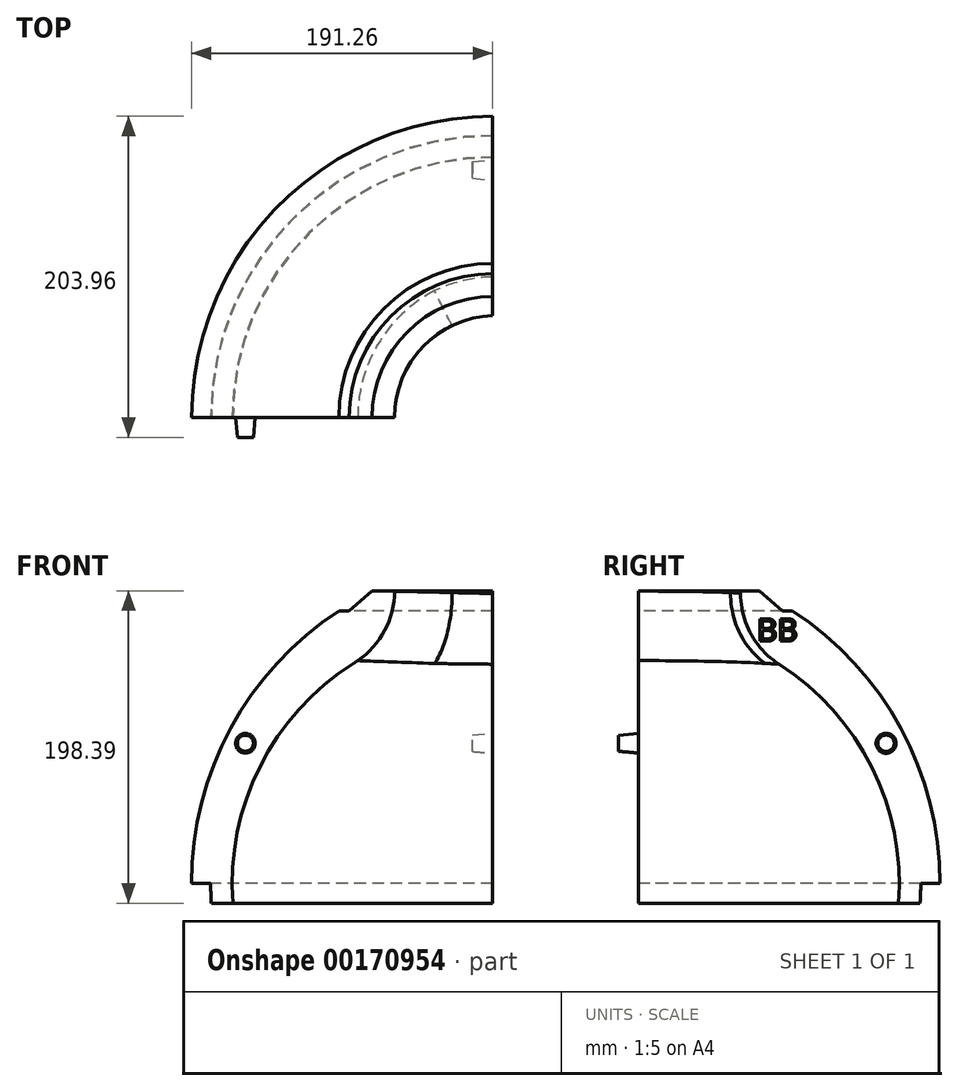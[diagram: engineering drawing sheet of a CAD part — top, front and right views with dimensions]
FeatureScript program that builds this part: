
annotation { "Feature Type Name" : "Feature", "Feature Type Description" : "" }
export const myFeature = defineFeature(function(context is Context, id is Id, definition is map)
    precondition{}
    {
        {
            var Q0;
            Q0=qCreatedBy(makeId("Front.planeOp"),FACE);
            var sketch = newSketch(context, id + "F0", { "sketchPlane" : qUnion([Q0])});
            skLineSegment(sketch, "E0", {"start": v(30.93, 103.48) * mm, "end": v(-45.8, 103.48) * mm});
            skLineSegment(sketch, "E1", {"start": v(30.93, 103.48) * mm, "end": v(30.93, 83.03) * mm});
            skLineSegment(sketch, "E2", {"start": v(-45.8, 103.48) * mm, "end": v(-60.28, 90.79) * mm});
            skLineSegment(sketch, "E3", {"start": v(30.93, -61.93) * mm, "end": v(-133.25, -61.93) * mm});
            skLineSegment(sketch, "E4", {"start": v(-147.77, -94.91) * mm, "end": v(-134.06, -94.91) * mm});
            skLineSegment(sketch, "E5", {"start": v(-160.33, -82.21) * mm, "end": v(-148.2, -82.22) * mm});
            skArc(sketch, "E6", {"start": v(-57.6, 57.35) * mm, "mid": v(-108.8, 6.19) * mm, "end": v(-133.25, -61.93) * mm});
            skArc(sketch, "E7.trimOffspring", {"start": v(-148.2, -82.22) * mm, "mid": v(-148.1, -88.57) * mm, "end": v(-147.77, -94.91) * mm});
            skLineSegment(sketch, "E8", {"start": v(30.93, 83.03) * mm, "end": v(30.93, -61.93) * mm});
            skLineSegment(sketch, "E9", {"start": v(-18.26, 103.48) * mm, "end": v(-18.26, 103.48) * mm});
            skArc(sketch, "E10", {"start": v(-66.85, 90.79) * mm, "mid": v(-135.53, 16.14) * mm, "end": v(-160.33, -82.21) * mm});
            skArc(sketch, "E11.filletArc", {"start": v(-57.6, 57.35) * mm, "mid": v(-34.45, 77.44) * mm, "end": v(-18.26, 103.48) * mm});
            skArc(sketch, "E12", {"start": v(-133.25, -61.93) * mm, "mid": v(-134.48, -78.4) * mm, "end": v(-134.06, -94.91) * mm});
            skLineSegment(sketch, "E13", {"start": v(-60.28, 90.79) * mm, "end": v(-66.85, 90.79) * mm});
            skSolve(sketch);
        }
        {
            var Q0;
            {var subQ0=sQuery(id+"F0.wireOp",EDGE,"E2");Q0=makeQuery(id+"F0.imprint","IMPRINT",FACE,{"disambiguationData":[TD([[makeQuery(id+"F0.imprint","IMPRINT",EDGE,{"derivedFrom":subQ0}),1.0]])]});}
            var Q1;
            Q1=sQuery(id+"F0.wireOp",EDGE,"E8");
            revolve(context, id + "F1", {"entities" : qUnion([Q0]), "axis" : qUnion([Q1]), "revolveType" : RevolveType.ONE_DIRECTION, "angle" : 90 * degree});
        }
        {
            var Q0;
            Q0=makeQuery(id+"F1.opRevolve","CAP_FACE",FACE,{"disambiguationData":[OSD([sQuery(id+"F0.wireOp",EDGE,"E0"),sQuery(id+"F0.wireOp",EDGE,"8f814b49-d637-47c4-8b9a-070ca617951d"),sQuery(id+"F0.wireOp",EDGE,"E2"),sQuery(id+"F0.wireOp",EDGE,"bb9fcc6d-65a5-43b8-a665-45e836ea0d68"),sQuery(id+"F0.wireOp",EDGE,"E4"),sQuery(id+"F0.wireOp",EDGE,"E5"),sQuery(id+"F0.wireOp",EDGE,"E6"),sQuery(id+"F0.wireOp",EDGE,"3126052c-2f44-435f-8919-2bff36e23e4e.trimOffspring"),sQuery(id+"F0.wireOp",EDGE,"E7.trimOffspring"),sQuery(id+"F0.wireOp",EDGE,"E9"),sQuery(id+"F0.wireOp",EDGE,"E10")])],"isStart":true});
            var sketch = newSketch(context, id + "F2", { "sketchPlane" : qUnion([Q0])});
            skCircle(sketch, "E14", {"center": v(-126.16, 6.69) * mm, "radius": 6.22 * mm});
            skSolve(sketch);
        }
        {
            var Q0;
            Q0 = qSketchRegion(id + "F2", true);
            extrude(context, id + "F3", {"entities" : qUnion([Q0]), "operationType" : NewBodyOperationType.ADD, "depth" : 12.7 * mm, "hasDraft" : true, "draftAngle" : 5 * degree, "draftPullDirection" : true});
        }
        {
            var Q0;
            Q0=makeQuery(id+"F1.opRevolve","CAP_FACE",FACE,{"disambiguationData":[OSD([sQuery(id+"F0.wireOp",EDGE,"E0"),sQuery(id+"F0.wireOp",EDGE,"8f814b49-d637-47c4-8b9a-070ca617951d"),sQuery(id+"F0.wireOp",EDGE,"E2"),sQuery(id+"F0.wireOp",EDGE,"bb9fcc6d-65a5-43b8-a665-45e836ea0d68"),sQuery(id+"F0.wireOp",EDGE,"E4"),sQuery(id+"F0.wireOp",EDGE,"E5"),sQuery(id+"F0.wireOp",EDGE,"E6"),sQuery(id+"F0.wireOp",EDGE,"3126052c-2f44-435f-8919-2bff36e23e4e.trimOffspring"),sQuery(id+"F0.wireOp",EDGE,"E7.trimOffspring"),sQuery(id+"F0.wireOp",EDGE,"E9"),sQuery(id+"F0.wireOp",EDGE,"E10")])],"isStart":false});
            var sketch = newSketch(context, id + "F4", { "sketchPlane" : qUnion([Q0])});
            skCircle(sketch, "E15", {"center": v(157.1, 6.69) * mm, "radius": 6.35 * mm});
            skSolve(sketch);
        }
        {
            var Q0;
            Q0 = qSketchRegion(id + "F4", true);
            extrude(context, id + "F5", {"entities" : qUnion([Q0]), "operationType" : NewBodyOperationType.REMOVE, "oppositeDirection" : true, "depth" : 12.7 * mm, "hasDraft" : true, "draftAngle" : 5 * degree, "draftPullDirection" : true});
        }
        {
            var Q0;
            Q0=qCreatedBy(makeId("Top.planeOp"),FACE);
            var sketch = newSketch(context, id + "F6", { "sketchPlane" : qUnion([Q0])});
            skCircle(sketch, "E16", {"center": v(33.28, 0) * mm, "radius": 64.74 * mm});
            skSolve(sketch);
        }
        {
            var Q0;
            Q0 = qSketchRegion(id + "F6", true);
            extrude(context, id + "F7", {"entities" : qUnion([Q0]), "operationType" : NewBodyOperationType.REMOVE, "endBound" : BoundingType.THROUGH_ALL, "depth" : 25.4 * mm});
        }
        {
            var Q0;
            Q0=makeQuery(id+"F7.boolean.opBoolean","INTERSECT",EDGE,{"derivedFrom":[makeQuery(id+"F1.opRevolve","SWEPT_FACE",FACE,{"disambiguationData":[OSD([sQuery(id+"F0.wireOp",EDGE,"E11.filletArc")])]}),makeQuery(id+"F7.opExtrude","SWEPT_FACE",FACE,{"disambiguationData":[OSD([sQuery(id+"F6.wireOp",EDGE,"E16")])]})]});
            fillet(context, id + "F8", {"entities" : qUnion([Q0]), "radius" : 53.34 * mm, "tangentPropagation" : true, "allowEdgeOverflow" : false});
        }
        {
            var Q0;
            Q0=makeQuery(id+"F1.opRevolve","CAP_FACE",FACE,{"disambiguationData":[OSD([sQuery(id+"F0.wireOp",EDGE,"E0"),sQuery(id+"F0.wireOp",EDGE,"E2"),sQuery(id+"F0.wireOp",EDGE,"E4"),sQuery(id+"F0.wireOp",EDGE,"E5"),sQuery(id+"F0.wireOp",EDGE,"E6"),sQuery(id+"F0.wireOp",EDGE,"E7.trimOffspring"),sQuery(id+"F0.wireOp",EDGE,"E10"),sQuery(id+"F0.wireOp",EDGE,"E11.filletArc"),sQuery(id+"F0.wireOp",EDGE,"E12"),sQuery(id+"F0.wireOp",EDGE,"E13")])],"isStart":false});
            var sketch = newSketch(context, id + "F9", { "sketchPlane" : qUnion([Q0])});
            skSolve(sketch);
        }
        {
            var Q0;
            {var subQ8=sQuery(id+"F0.wireOp",EDGE,"E2");Q0=makeQuery(id+"F9.imprint","IMPRINT",FACE,{"disambiguationData":[TD([[makeQuery(id+"F9.imprint","IMPRINT",EDGE,{"derivedFrom":makeQuery(id+"F1.opRevolve","CAP_EDGE",EDGE,{"disambiguationData":[OSD([subQ8])],"isStart":false})}),-1.0]])]});}
            var sketch = newSketch(context, id + "F10", { "sketchPlane" : qUnion([Q0])});
            skText(sketch, "E17", { "text": "BB", "fontName": "OpenSans-Regular.ttf"});
            const initialGuessF10  = {"E17": [0.07515, 0.0716, 1, 0, 0.01432]};
            skSetInitialGuess(sketch, initialGuessF10);
            skSolve(sketch);
        }
        {
            var Q0;
            Q0 = qSketchRegion(id + "F10", true);
            extrude(context, id + "F11", {"entities" : qUnion([Q0]), "operationType" : NewBodyOperationType.REMOVE, "oppositeDirection" : true, "depth" : 0.25 * mm});
        }
        {
            var Q0;
            Q0 = qSketchRegion(id + "F10", true);
            extrude(context, id + "F12", {"entities" : qUnion([Q0]), "operationType" : NewBodyOperationType.REMOVE, "oppositeDirection" : true, "depth" : 0.25 * mm});
        }
    });
